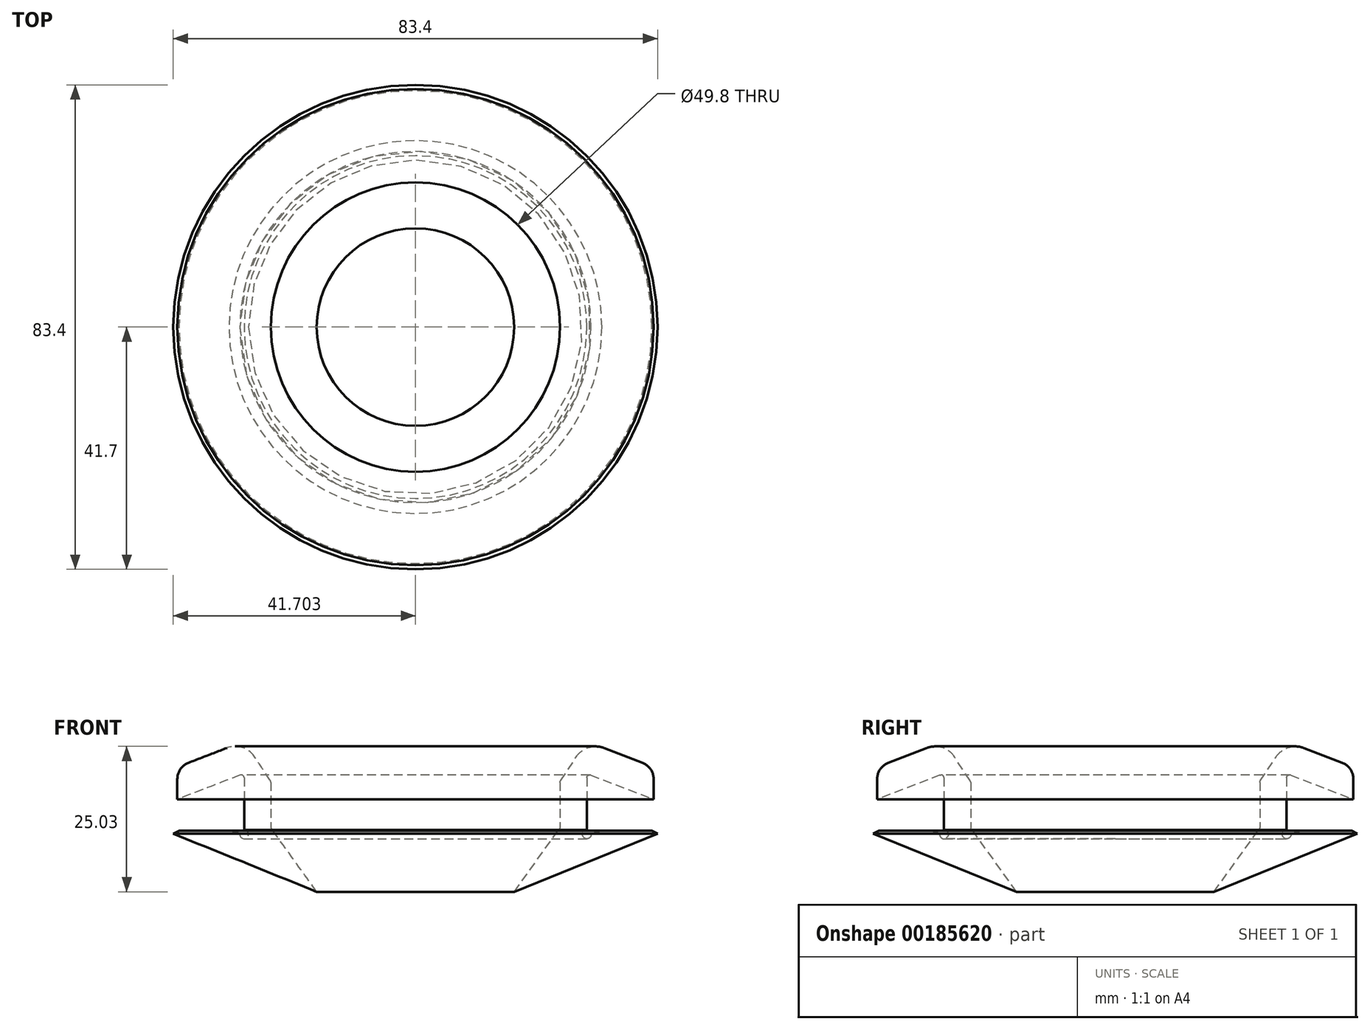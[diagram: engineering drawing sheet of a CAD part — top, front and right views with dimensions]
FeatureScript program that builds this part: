
annotation { "Feature Type Name" : "Feature", "Feature Type Description" : "" }
export const myFeature = defineFeature(function(context is Context, id is Id, definition is map)
    precondition{}
    {
        {
            var Q0;
            Q0=qCreatedBy(makeId("Front.planeOp"),FACE);
            var sketch = newSketch(context, id + "F0", { "sketchPlane" : qUnion([Q0])});
            skLineSegment(sketch, "E0.left", {"start": v(77.26, 11.73) * mm, "end": v(77.26, 4.04) * mm});
            skLineSegment(sketch, "E0.right", {"start": v(81.86, 12.5) * mm, "end": v(81.86, 3.5) * mm});
            skLineSegment(sketch, "E1", {"start": v(82.54, 12.98) * mm, "end": v(93.36, 8.8) * mm});
            skLineSegment(sketch, "E2", {"start": v(93.36, 8.8) * mm, "end": v(93.36, 12.3) * mm});
            skLineSegment(sketch, "E3", {"start": v(91.44, 15.1) * mm, "end": v(84.84, 17.64) * mm});
            skLineSegment(sketch, "E4", {"start": v(77.35, 12) * mm, "end": v(80.06, 16.11) * mm});
            skArc(sketch, "E5.filletArc", {"start": v(93.36, 12.3) * mm, "mid": v(92.84, 14) * mm, "end": v(91.44, 15.1) * mm});
            skPoint(sketch, "E6.visualSharp", {"position": v(81.84, 18.8) * mm});
            skLineSegment(sketch, "E7", {"start": v(77.17, 3.75) * mm, "end": v(69.36, -7.12) * mm});
            skLineSegment(sketch, "E8", {"start": v(69.36, -7.12) * mm, "end": v(94.06, 2.88) * mm});
            skPoint(sketch, "E9", {"position": v(92.84, 14) * mm});
            skArc(sketch, "E10.filletArc", {"start": v(84.84, 17.64) * mm, "mid": v(82.18, 17.72) * mm, "end": v(80.06, 16.11) * mm});
            skPoint(sketch, "E11.visualSharp", {"position": v(77.26, 11.88) * mm});
            skArc(sketch, "E11.filletArc", {"start": v(77.35, 12) * mm, "mid": v(77.28, 11.87) * mm, "end": v(77.26, 11.73) * mm});
            skPoint(sketch, "E12.visualSharp", {"position": v(77.26, 3.88) * mm});
            skArc(sketch, "E12.filletArc", {"start": v(77.17, 3.75) * mm, "mid": v(77.24, 3.89) * mm, "end": v(77.26, 4.04) * mm});
            skPoint(sketch, "E13", {"position": v(93.06, 3.38) * mm});
            skLineSegment(sketch, "E14", {"start": v(84.46, 3.38) * mm, "end": v(93.06, 3.38) * mm});
            skLineSegment(sketch, "E15", {"start": v(93.06, 3.38) * mm, "end": v(94.06, 2.88) * mm});
            skPoint(sketch, "E16.visualSharp", {"position": v(81.86, 13.24) * mm});
            skArc(sketch, "E16.filletArc", {"start": v(82.54, 12.98) * mm, "mid": v(82.08, 12.92) * mm, "end": v(81.86, 12.5) * mm});
            skPoint(sketch, "E17", {"position": v(83.14, 17.9) * mm});
            skLineSegment(sketch, "E18", {"start": v(84.46, 3.38) * mm, "end": v(82.6, 2.93) * mm});
            skArc(sketch, "E19", {"start": v(81.86, 3.5) * mm, "mid": v(81.4, 2.17) * mm, "end": v(82.6, 2.93) * mm});
            skLineSegment(sketch, "E20", {"start": v(52.36, -7.12) * mm, "end": v(52.36, 24.81) * mm});
            skSolve(sketch);
        }
        {
            var Q0;
            Q0=makeQuery(id+"F0.imprint","IMPRINT",FACE,{"disambiguationData":[TD([[makeQuery(id+"F0.imprint","IMPRINT",EDGE,{"derivedFrom":sQuery(id+"F0.wireOp",EDGE,"E0.left")}),1.0]])]});
            var Q1;
            Q1=sQuery(id+"F0.wireOp",EDGE,"E20");
            revolve(context, id + "F1", {"entities" : qUnion([Q0]), "axis" : qUnion([Q1]), "revolveType" : RevolveType.FULL});
        }
    });
